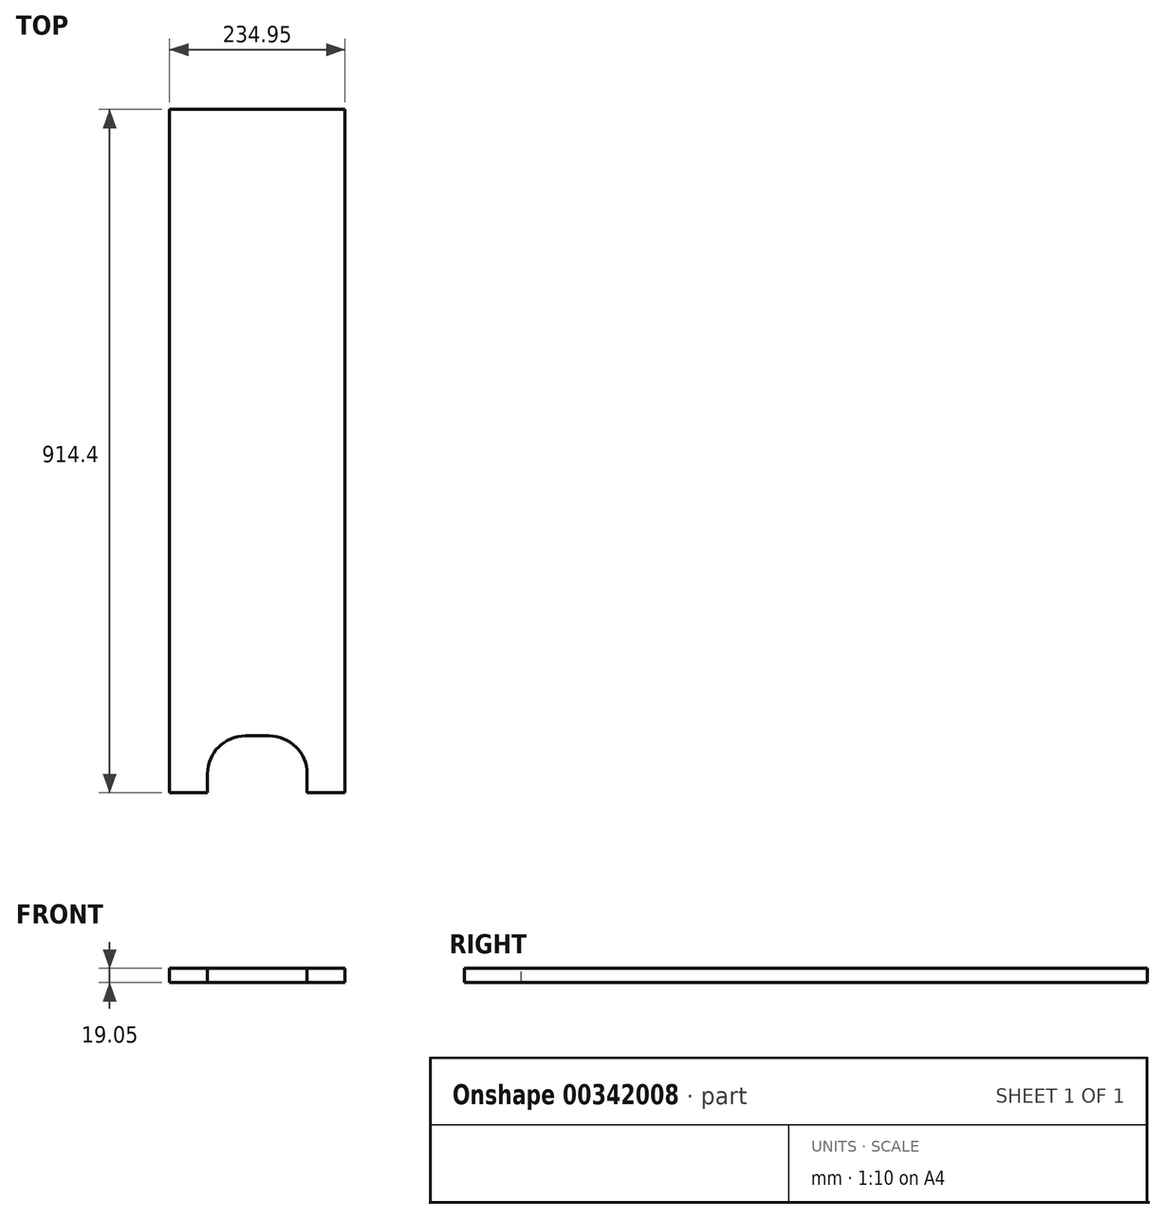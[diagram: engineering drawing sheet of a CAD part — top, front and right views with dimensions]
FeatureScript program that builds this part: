
annotation { "Feature Type Name" : "Feature", "Feature Type Description" : "" }
export const myFeature = defineFeature(function(context is Context, id is Id, definition is map)
    precondition{}
    {
        {
            var Q0;
            Q0=qCreatedBy(makeId("Top.planeOp"),FACE);
            var sketch = newSketch(context, id + "F0", { "sketchPlane" : qUnion([Q0])});
            skLineSegment(sketch, "E0.bottom", {"start": v(0, 0) * mm, "end": v(234.95, 0) * mm});
            skLineSegment(sketch, "E0.top", {"start": v(0, -914.4) * mm, "end": v(234.95, -914.4) * mm});
            skLineSegment(sketch, "E0.left", {"start": v(0, 0) * mm, "end": v(0, -914.4) * mm});
            skLineSegment(sketch, "E0.right", {"start": v(234.95, 0) * mm, "end": v(234.95, -914.4) * mm});
            skSolve(sketch);
        }
        {
            var Q0;
            Q0=makeQuery(id+"F0.imprint","IMPRINT",FACE,{"disambiguationData":[TD([[makeQuery(id+"F0.imprint","IMPRINT",EDGE,{"derivedFrom":sQuery(id+"F0.wireOp",EDGE,"E0.bottom")}),-1.0]])]});
            extrude(context, id + "F1", {"entities" : qUnion([Q0]), "depth" : 19.05 * mm});
        }
        {
            var Q0;
            Q0=makeQuery(id+"F1.opExtrude","CAP_FACE",FACE,{"disambiguationData":[OSD([sQuery(id+"F0.wireOp",EDGE,"E0.bottom"),sQuery(id+"F0.wireOp",EDGE,"E0.top"),sQuery(id+"F0.wireOp",EDGE,"E0.left"),sQuery(id+"F0.wireOp",EDGE,"E0.right")])],"isStart":false});
            var sketch = newSketch(context, id + "F2", { "sketchPlane" : qUnion([Q0])});
            skLineSegment(sketch, "E1.bottom", {"start": v(50.8, -914.4) * mm, "end": v(184.15, -914.4) * mm});
            skLineSegment(sketch, "E1.top", {"start": v(50.8, -838.2) * mm, "end": v(184.15, -838.2) * mm});
            skLineSegment(sketch, "E1.left", {"start": v(50.8, -914.4) * mm, "end": v(50.8, -838.2) * mm});
            skLineSegment(sketch, "E1.right", {"start": v(184.15, -914.4) * mm, "end": v(184.15, -838.2) * mm});
            skSolve(sketch);
        }
        {
            var Q0;
            Q0=makeQuery(id+"F2.imprint","IMPRINT",FACE,{"disambiguationData":[TD([[makeQuery(id+"F2.imprint","IMPRINT",EDGE,{"derivedFrom":sQuery(id+"F2.wireOp",EDGE,"E1.bottom")}),1.0]])]});
            extrude(context, id + "F3", {"entities" : qUnion([Q0]), "operationType" : NewBodyOperationType.REMOVE, "oppositeDirection" : true, "depth" : 19.05 * mm});
        }
        {
            var Q0;
            Q0=makeQuery(id+"F3.boolean.opBoolean","COPY",EDGE,{"derivedFrom":makeQuery(id+"F3.opExtrude","SWEPT_EDGE",EDGE,{"disambiguationData":[OSD([sQuery(id+"F2.wireOp",EDGE,"E1.top"),sQuery(id+"F2.wireOp",EDGE,"E1.left")])]})});
            var Q1;
            Q1=makeQuery(id+"F3.boolean.opBoolean","COPY",EDGE,{"derivedFrom":makeQuery(id+"F3.opExtrude","SWEPT_EDGE",EDGE,{"disambiguationData":[OSD([sQuery(id+"F2.wireOp",EDGE,"E1.top"),sQuery(id+"F2.wireOp",EDGE,"E1.right")])]})});
            fillet(context, id + "F4", {"entities" : qUnion([Q0, Q1]), "radius" : 50.8 * mm, "tangentPropagation" : true, "allowEdgeOverflow" : false});
        }
    });
